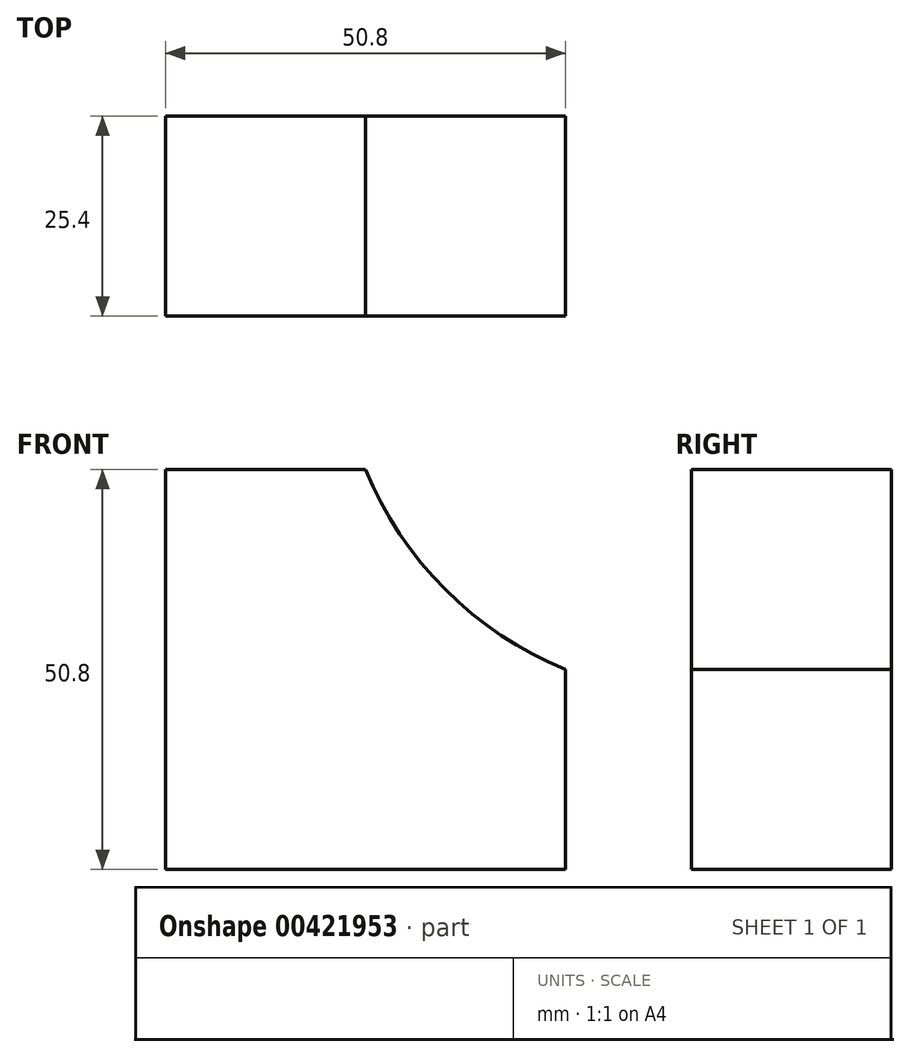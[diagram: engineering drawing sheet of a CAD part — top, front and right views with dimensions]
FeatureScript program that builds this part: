
annotation { "Feature Type Name" : "Feature", "Feature Type Description" : "" }
export const myFeature = defineFeature(function(context is Context, id is Id, definition is map)
    precondition{}
    {
        {
            var Q0;
            Q0=qCreatedBy(makeId("Front.planeOp"),FACE);
            var sketch = newSketch(context, id + "F0", { "sketchPlane" : qUnion([Q0])});
            skLineSegment(sketch, "E0", {"start": v(-50.8, 0) * mm, "end": v(-50.8, 50.8) * mm});
            skLineSegment(sketch, "E1", {"start": v(-50.8, 50.8) * mm, "end": v(-25.4, 50.8) * mm});
            skLineSegment(sketch, "E2", {"start": v(0, 25.4) * mm, "end": v(0, 0) * mm});
            skArc(sketch, "E3", {"start": v(-25.4, 50.8) * mm, "mid": v(-15.26, 35.54) * mm, "end": v(0, 25.4) * mm});
            skLineSegment(sketch, "E4", {"start": v(-50.8, 0) * mm, "end": v(0, 0) * mm});
            skSolve(sketch);
        }
        {
            var Q0;
            Q0=makeQuery(id+"F0.imprint","IMPRINT",FACE,{"disambiguationData":[TD([[makeQuery(id+"F0.imprint","IMPRINT",EDGE,{"derivedFrom":sQuery(id+"F0.wireOp",EDGE,"E0")}),-1.0]])]});
            extrude(context, id + "F1", {"entities" : qUnion([Q0]), "depth" : 25.4 * mm});
        }
    });
